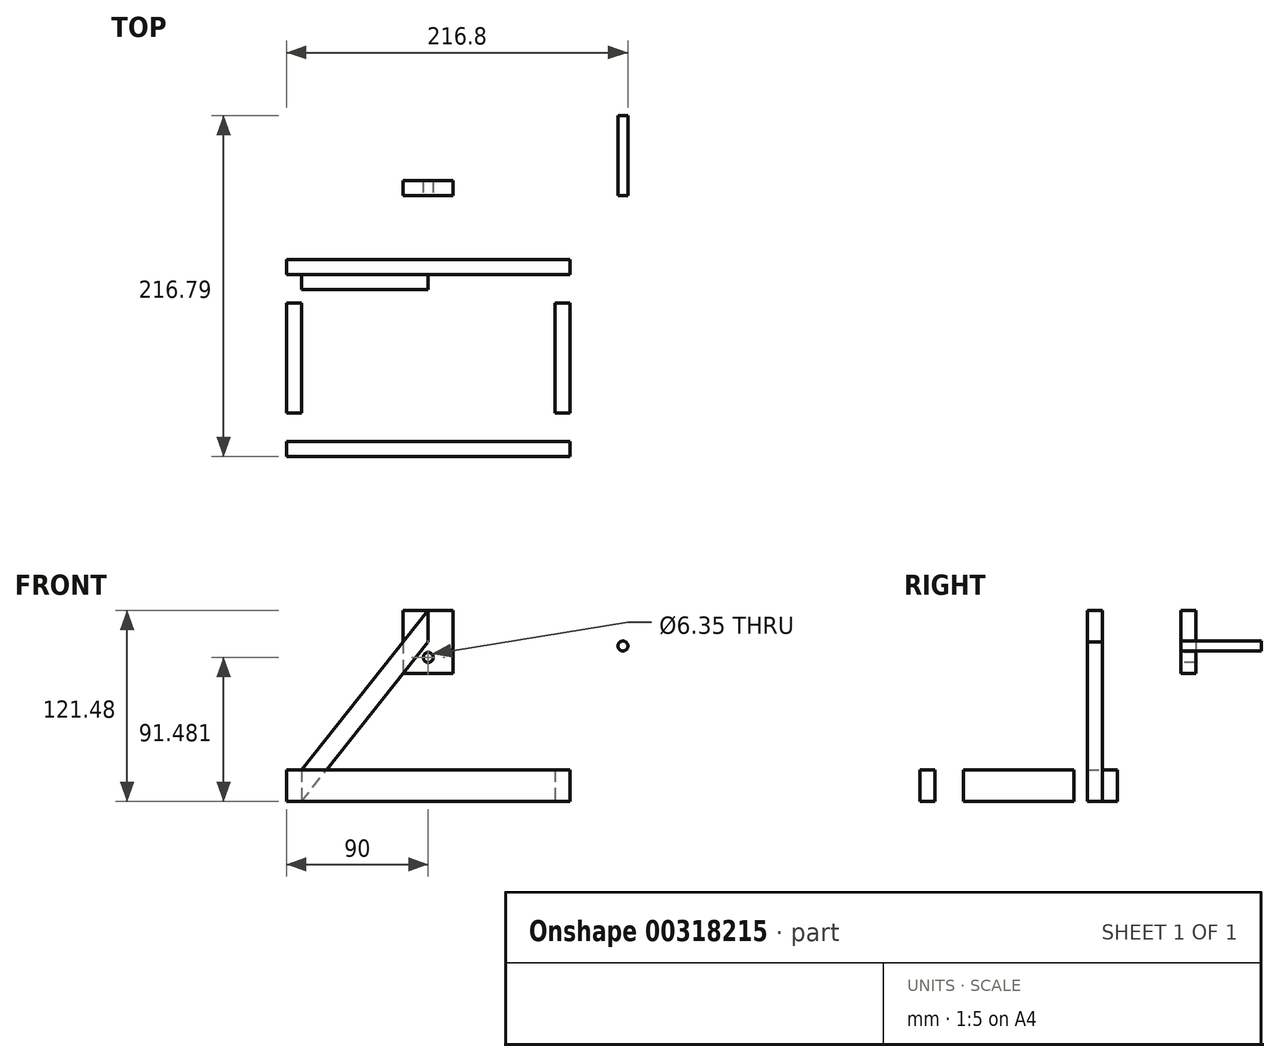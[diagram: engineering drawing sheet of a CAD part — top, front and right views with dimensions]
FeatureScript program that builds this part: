
annotation { "Feature Type Name" : "Feature", "Feature Type Description" : "" }
export const myFeature = defineFeature(function(context is Context, id is Id, definition is map)
    precondition{}
    {
        {
            assignVariable(context, id + "F0", {"name" : "thickness", "anyValue" : 9.52 * mm});
        }
        {
            var Q0;
            Q0=qCreatedBy(makeId("Top.planeOp"),FACE);
            var sketch = newSketch(context, id + "F1", { "sketchPlane" : qUnion([Q0])});
            skLineSegment(sketch, "E0.bottom", {"start": v(-150, 150) * mm, "end": v(150, 150) * mm, "construction": true});
            skLineSegment(sketch, "E0.top", {"start": v(-150, -150) * mm, "end": v(150, -150) * mm, "construction": true});
            skLineSegment(sketch, "E0.left", {"start": v(-150, 150) * mm, "end": v(-150, -150) * mm, "construction": true});
            skLineSegment(sketch, "E0.right", {"start": v(150, 150) * mm, "end": v(150, -150) * mm, "construction": true});
            skLineSegment(sketch, "E1", {"start": v(-150, 150) * mm, "end": v(150, -150) * mm, "construction": true});
            skPoint(sketch, "E2", {"position": v(0, 0) * mm});
            skLineSegment(sketch, "E3", {"start": v(150, 0) * mm, "end": v(-150, 0) * mm, "construction": true});
            skLineSegment(sketch, "E4", {"start": v(0, -150) * mm, "end": v(0, 150) * mm, "construction": true});
            skLineSegment(sketch, "E5.bottom", {"start": v(-90, 62.66) * mm, "end": v(90, 62.66) * mm});
            skLineSegment(sketch, "E5.top", {"start": v(-90, 53.13) * mm, "end": v(90, 53.13) * mm});
            skLineSegment(sketch, "E5.left", {"start": v(-90, 62.66) * mm, "end": v(-90, 53.13) * mm});
            skLineSegment(sketch, "E5.right", {"start": v(90, 62.66) * mm, "end": v(90, 53.13) * mm});
            skLineSegment(sketch, "E6.bottom", {"start": v(-90, 35) * mm, "end": v(-80.47, 35) * mm});
            skLineSegment(sketch, "E6.top", {"start": v(-90, -35) * mm, "end": v(-80.47, -35) * mm});
            skLineSegment(sketch, "E6.left", {"start": v(-90, 35) * mm, "end": v(-90, -35) * mm});
            skLineSegment(sketch, "E6.right", {"start": v(-80.47, 35) * mm, "end": v(-80.47, -35) * mm});
            skLineSegment(sketch, "E7.MirrorCS", {"start": v(-90, -53.13) * mm, "end": v(90, -53.13) * mm});
            skLineSegment(sketch, "E8.MirrorCS", {"start": v(-90, -62.66) * mm, "end": v(90, -62.66) * mm});
            skLineSegment(sketch, "E9.MirrorCS", {"start": v(-90, -62.66) * mm, "end": v(-90, -53.13) * mm});
            skLineSegment(sketch, "E10.MirrorCS", {"start": v(90, -62.66) * mm, "end": v(90, -53.13) * mm});
            skLineSegment(sketch, "E11.MirrorCS", {"start": v(90, 35) * mm, "end": v(90, -35) * mm});
            skLineSegment(sketch, "E12.MirrorCS", {"start": v(90, 35) * mm, "end": v(80.48, 35) * mm});
            skLineSegment(sketch, "E13.MirrorCS", {"start": v(80.48, 35) * mm, "end": v(80.48, -35) * mm});
            skLineSegment(sketch, "E14.MirrorCS", {"start": v(90, -35) * mm, "end": v(80.48, -35) * mm});
            skPoint(sketch, "E15", {"position": v(0, 53.13) * mm});
            skPoint(sketch, "E16", {"position": v(-80.47, 0) * mm});
            skLineSegment(sketch, "E17", {"start": v(-90, 62.66) * mm, "end": v(-90, -62.66) * mm, "construction": true});
            skLineSegment(sketch, "E18", {"start": v(90, 62.66) * mm, "end": v(90, -62.66) * mm, "construction": true});
            skSolve(sketch);
        }
        {
            var Q0;
            Q0=qSketchRegion(id+"F1",true);
            extrude(context, id + "F2", {"entities" : qUnion([Q0]), "depth" : 20 * mm});
        }
        {
            var Q0;
            Q0=makeQuery(id+"F2.opExtrude","SWEPT_FACE",FACE,{"disambiguationData":[OSD([sQuery(id+"F1.wireOp",EDGE,"E5.top")])]});
            var sketch = newSketch(context, id + "F3", { "sketchPlane" : qUnion([Q0])});
            skLineSegment(sketch, "E19", {"start": v(0, 0) * mm, "end": v(0, 121.48) * mm, "construction": true});
            skPoint(sketch, "E19.endSnap0", {"position": v(0, 0) * mm});
            skLineSegment(sketch, "E20.0.0", {"start": v(-80.47, 0) * mm, "end": v(-90, 0) * mm, "construction": true});
            skLineSegment(sketch, "E20.0.1", {"start": v(-90, 0) * mm, "end": v(-90, 20) * mm, "construction": true});
            skLineSegment(sketch, "E20.0.2", {"start": v(-90, 20) * mm, "end": v(-80.47, 20) * mm, "construction": true});
            skLineSegment(sketch, "E20.0.3", {"start": v(-80.47, 20) * mm, "end": v(-80.47, 0) * mm, "construction": true});
            skLineSegment(sketch, "E21.0", {"start": v(90, 20) * mm, "end": v(90, 0) * mm, "construction": true});
            skLineSegment(sketch, "E22.0.0", {"start": v(90, 0) * mm, "end": v(80.48, 0) * mm, "construction": true});
            skLineSegment(sketch, "E22.0.1", {"start": v(80.48, 0) * mm, "end": v(80.48, 20) * mm, "construction": true});
            skLineSegment(sketch, "E22.0.2", {"start": v(80.48, 20) * mm, "end": v(90, 20) * mm, "construction": true});
            skLineSegment(sketch, "E23", {"start": v(-80.47, 20) * mm, "end": v(-80.47, 0) * mm});
            skLineSegment(sketch, "E24", {"start": v(-80.47, 20) * mm, "end": v(0, 121.48) * mm});
            skLineSegment(sketch, "E25", {"start": v(-80.47, 0) * mm, "end": v(0, 101.48) * mm});
            skLineSegment(sketch, "E26", {"start": v(0, 101.48) * mm, "end": v(0, 121.48) * mm});
            skSolve(sketch);
        }
        {
            var Q0;
            Q0=qSketchRegion(id+"F3",true);
            extrude(context, id + "F4", {"entities" : qUnion([Q0]), "depth" : getVariable(context, 'thickness')});
        }
        {
            var Q0;
            Q0=makeQuery(id+"F4.opExtrude","CAP_FACE",FACE,{"disambiguationData":[OSD([sQuery(id+"F3.wireOp",EDGE,"E23"),sQuery(id+"F3.wireOp",EDGE,"E24"),sQuery(id+"F3.wireOp",EDGE,"E25"),sQuery(id+"F3.wireOp",EDGE,"E26")])],"isStart":true});
            cPlane(context, id + "F5", {"entities" : qUnion([Q0]), "cplaneType" : CPlaneType.OFFSET, "offset" : 50 * mm, "width" : 150 * mm, "height" : 150 * mm});
        }
        {
            var Q0;
            Q0=qCreatedBy(id+"F5.planeOp",FACE);
            var sketch = newSketch(context, id + "F6", { "sketchPlane" : qUnion([Q0])});
            skLineSegment(sketch, "E27.0", {"start": v(0, 101.48) * mm, "end": v(0, 121.48) * mm, "construction": true});
            skLineSegment(sketch, "E28.0", {"start": v(80.47, 20) * mm, "end": v(0, 121.48) * mm, "construction": true});
            skLineSegment(sketch, "E29.bottom", {"start": v(-15.86, 121.48) * mm, "end": v(15.86, 121.48) * mm});
            skLineSegment(sketch, "E29.top", {"start": v(-15.86, 81.48) * mm, "end": v(15.86, 81.48) * mm});
            skLineSegment(sketch, "E29.left", {"start": v(-15.86, 121.48) * mm, "end": v(-15.86, 81.48) * mm});
            skLineSegment(sketch, "E29.right", {"start": v(15.86, 121.48) * mm, "end": v(15.86, 81.48) * mm});
            skLineSegment(sketch, "E30.0", {"start": v(80.47, 0) * mm, "end": v(0, 101.48) * mm, "construction": true});
            skLineSegment(sketch, "E31", {"start": v(0, 81.48) * mm, "end": v(0, 121.48) * mm, "construction": true});
            skCircle(sketch, "E32", {"center": v(0, 91.48) * mm, "radius": 3.18 * mm});
            skSolve(sketch);
        }
        {
            var Q0;
            Q0=qSketchRegion(id+"F6",true);
            extrude(context, id + "F7", {"entities" : qUnion([Q0]), "depth" : getVariable(context, 'thickness')});
        }
        {
            var Q0;
            Q0=qCreatedBy(id+"F5.planeOp",FACE);
            var sketch = newSketch(context, id + "F8", { "sketchPlane" : qUnion([Q0])});
            skCircle(sketch, "E33", {"center": v(-123.62, 98.75) * mm, "radius": 3.18 * mm});
            skSolve(sketch);
        }
        {
            var Q0;
            Q0=qSketchRegion(id+"F8",true);
            extrude(context, id + "F9", {"entities" : qUnion([Q0]), "depth" : 51 * mm});
        }
        {
            var Q0;
            Q0=makeQuery(id+"F4.opExtrude","SWEPT_BODY",BODY,{"disambiguationData":[OSD([sQuery(id+"F3.wireOp",EDGE,"E23"),sQuery(id+"F3.wireOp",EDGE,"E24"),sQuery(id+"F3.wireOp",EDGE,"E25"),sQuery(id+"F3.wireOp",EDGE,"E26")])]});
            var Q1;
            Q1=makeQuery(id+"F4.opExtrude","SWEPT_FACE",FACE,{"disambiguationData":[OSD([sQuery(id+"F3.wireOp",EDGE,"E26")])]});
            mirror(context, id + "F10", {"entities" : qUnion([Q0]), "mirrorPlane" : qUnion([Q1])});
        }
        {
            var Q0;
            Q0=makeQuery(id+"F10.opPattern","COPY",BODY,{"derivedFrom":makeQuery(id+"F4.opExtrude","SWEPT_BODY",BODY,{"disambiguationData":[OSD([sQuery(id+"F3.wireOp",EDGE,"E23"),sQuery(id+"F3.wireOp",EDGE,"E24"),sQuery(id+"F3.wireOp",EDGE,"E25"),sQuery(id+"F3.wireOp",EDGE,"E26")])]}),"instanceName":"1"});
            deleteBodies(context, id + "F12", {"entities" : qUnion([Q0])});
        }
    });
